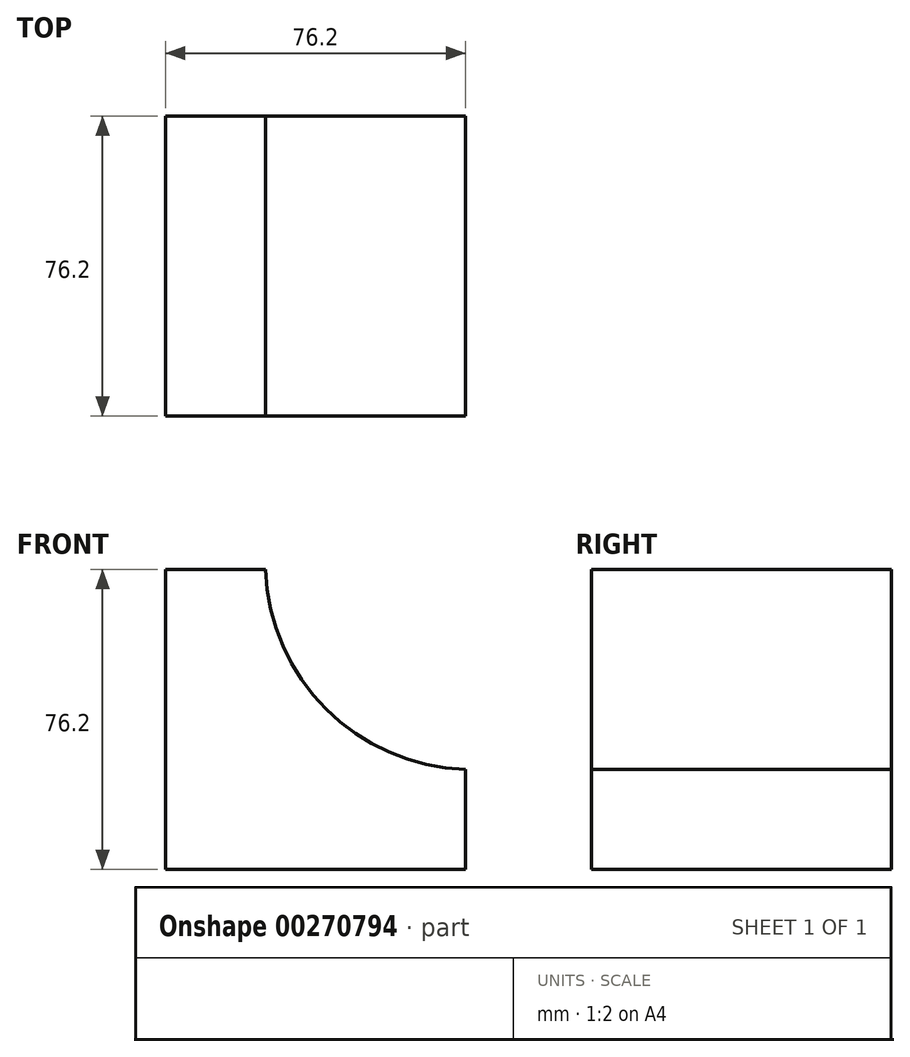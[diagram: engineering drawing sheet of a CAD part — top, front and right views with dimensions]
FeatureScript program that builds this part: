
annotation { "Feature Type Name" : "Feature", "Feature Type Description" : "" }
export const myFeature = defineFeature(function(context is Context, id is Id, definition is map)
    precondition{}
    {
        {
            var Q0;
            Q0=qCreatedBy(makeId("Front.planeOp"),FACE);
            var sketch = newSketch(context, id + "F0", { "sketchPlane" : qUnion([Q0])});
            skLineSegment(sketch, "E0", {"start": v(-40.66, 42.31) * mm, "end": v(-40.66, -33.89) * mm});
            skLineSegment(sketch, "E1", {"start": v(-40.66, -33.89) * mm, "end": v(35.54, -33.89) * mm});
            skLineSegment(sketch, "E2", {"start": v(35.54, -33.89) * mm, "end": v(35.54, -8.49) * mm});
            skLineSegment(sketch, "E3", {"start": v(-40.66, 42.31) * mm, "end": v(-15.26, 42.31) * mm});
            skArc(sketch, "E4", {"start": v(-15.26, 42.31) * mm, "mid": v(0.11, 6.9) * mm, "end": v(35.54, -8.49) * mm});
            skSolve(sketch);
        }
        {
            var Q0;
            Q0 = qSketchRegion(id + "F0", true);
            extrude(context, id + "F1", {"entities" : qUnion([Q0]), "depth" : 76.2 * mm});
        }
    });
